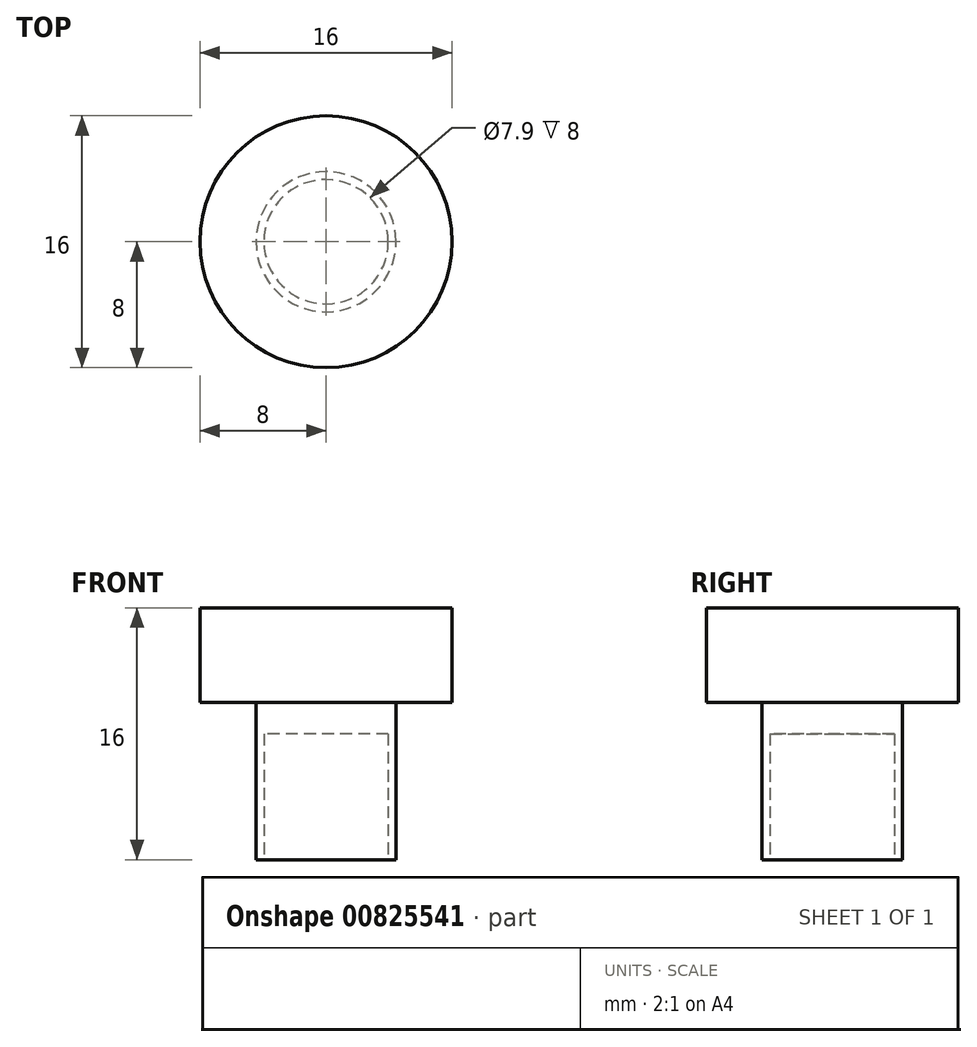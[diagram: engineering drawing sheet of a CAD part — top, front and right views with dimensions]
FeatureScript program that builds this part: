
annotation { "Feature Type Name" : "Feature", "Feature Type Description" : "" }
export const myFeature = defineFeature(function(context is Context, id is Id, definition is map)
    precondition{}
    {
        {
            var Q0;
            Q0=qCreatedBy(makeId("Top.planeOp"),FACE);
            var sketch = newSketch(context, id + "F0", { "sketchPlane" : qUnion([Q0])});
            skCircle(sketch, "E0", {"center": v(0, 0) * mm, "radius": 4.45 * mm});
            skCircle(sketch, "E1", {"center": v(0, 0) * mm, "radius": 3.95 * mm});
            skSolve(sketch);
        }
        {
            var Q0;
            Q0 = qSketchRegion(id + "F0", true);
            var Q1;
            Q1=makeQuery(id+"F0.imprint","IMPRINT",FACE,{"disambiguationData":[TD([[makeQuery(id+"F0.imprint","IMPRINT",EDGE,{"derivedFrom":sQuery(id+"F0.wireOp",EDGE,"gQIlikyk-XsJC-OwSO-pj1H-ld4xPt6BM2gG")}),1.0]])]});
            extrude(context, id + "F1", {"entities" : qUnion([Q0, Q1]), "depth" : 8 * mm, "offsetDistance" : 25 * mm});
        }
        {
            var Q0;
            Q0=makeQuery(id+"F1.opExtrude","CAP_FACE",FACE,{"disambiguationData":[OSD([sQuery(id+"F0.wireOp",EDGE,"E0"),sQuery(id+"F0.wireOp",EDGE,"E1")])],"isStart":false});
            var sketch = newSketch(context, id + "F2", { "sketchPlane" : qUnion([Q0])});
            skCircle(sketch, "E2", {"center": v(0, 0) * mm, "radius": 4.45 * mm});
            skSolve(sketch);
        }
        {
            var Q0;
            Q0 = qSketchRegion(id + "F2", true);
            extrude(context, id + "F3", {"entities" : qUnion([Q0]), "operationType" : NewBodyOperationType.ADD, "depth" : 2 * mm, "offsetDistance" : 25 * mm});
        }
        {
            var Q0;
            Q0=makeQuery(id+"F3.opExtrude","CAP_FACE",FACE,{"disambiguationData":[OSD([sQuery(id+"F2.wireOp",EDGE,"E2")])],"isStart":false});
            var sketch = newSketch(context, id + "F4", { "sketchPlane" : qUnion([Q0])});
            skCircle(sketch, "E3", {"center": v(0, 0) * mm, "radius": 8 * mm});
            skSolve(sketch);
        }
        {
            var Q0;
            Q0 = qSketchRegion(id + "F4", true);
            extrude(context, id + "F5", {"entities" : qUnion([Q0]), "operationType" : NewBodyOperationType.ADD, "depth" : 6 * mm, "offsetDistance" : 25 * mm});
        }
    });
